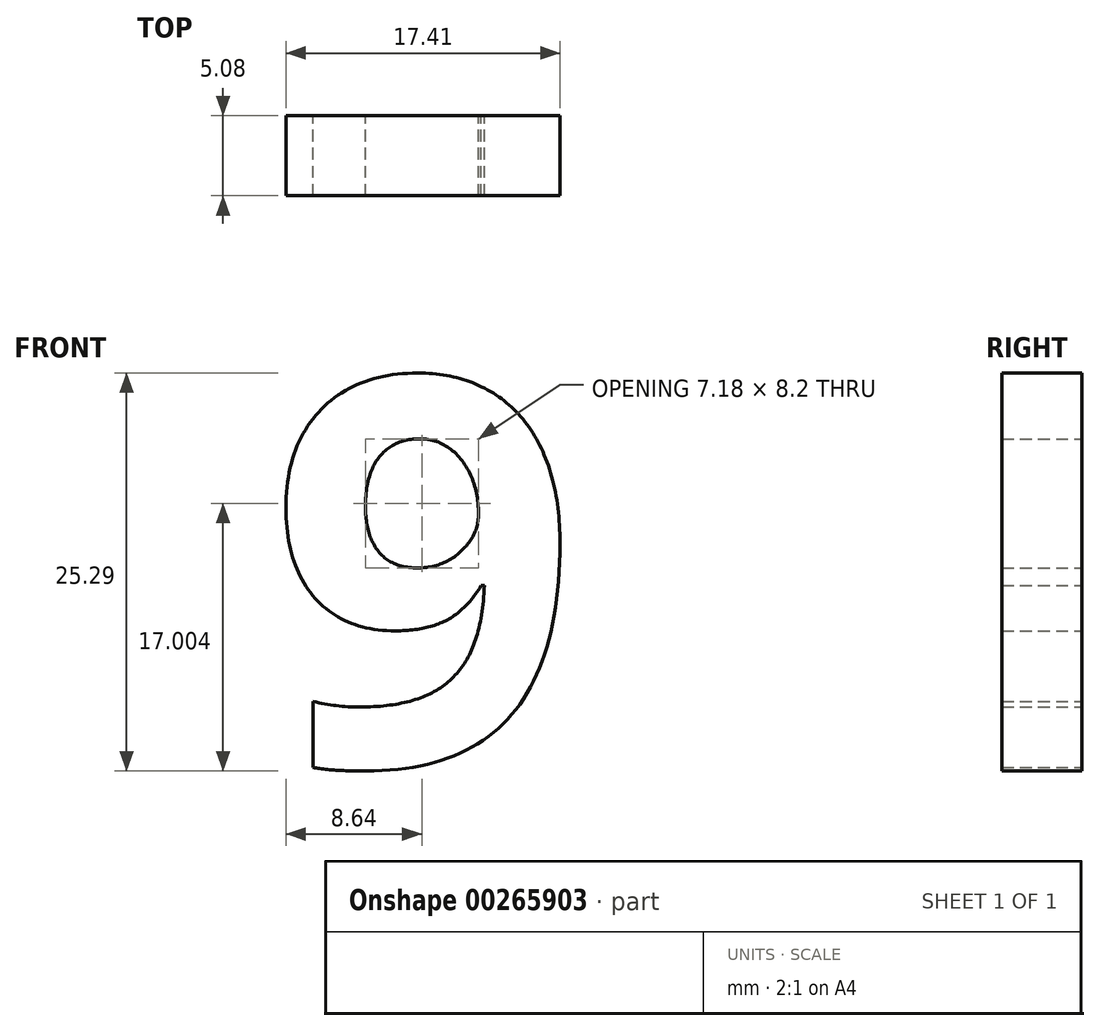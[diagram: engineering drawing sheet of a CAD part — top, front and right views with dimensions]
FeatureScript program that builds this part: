
annotation { "Feature Type Name" : "Feature", "Feature Type Description" : "" }
export const myFeature = defineFeature(function(context is Context, id is Id, definition is map)
    precondition{}
    {
        {
            var Q0;
            Q0=qCreatedBy(makeId("Front.planeOp"),FACE);
            var sketch = newSketch(context, id + "F0", { "sketchPlane" : qUnion([Q0])});
            skText(sketch, "E0", { "text": "9", "fontName": "OpenSans-Bold.ttf"});
            const initialGuessF0  = {"E0": [-0.02076, 0.0251, 1, 0, 0.02487]};
            skSetInitialGuess(sketch, initialGuessF0);
            skSolve(sketch);
        }
        {
            var Q0;
            Q0 = qSketchRegion(id + "F0", true);
            extrude(context, id + "F1", {"entities" : qUnion([Q0]), "depth" : 5.08 * mm});
        }
    });
